# Revit family: Faucet-Kitchen_Sink-KOHLER-Artifacts-K-76519
name_source: partatom
category: Plumbing Fixtures
revit_build: Autodesk Revit 2015 (Build: 20140606_1530(x64)
units: mm (PartAtom-declared; Revit-internal decimal feet)

## types (8) — shared parameters
ADA Compliant = Yes
Assembly Code = D2020
CW Connection = Yes
Cold Water Inlet = Cold Water Inlet
Date Modified = 03/16/2018
Default Elevation = 36"
Faucet Hole Spacing = 8"
Flow Rate = 2 GPM
HW Connection = Yes
Height = 13 1/2"
Hot Water Inlet = Hot Water Inlet
Length = 8 1/2"
Manufacturer = KOHLER Co.
MasterFormat 1995 = 15410
MasterFormat 2004 = 22.41.39
Material = Premium Metal Construction
Pressure = 60.00 psi
Product Documentation Link = http://www.us.kohler.com
Product Name = Artifacts
Product Page URL = http://www.us.kohler.com
Spout Reach = 8 1/2"
URL = https://www.us.kohler.com
Vent Connection = No
Waste Connection = No
Waste Water Outlet = Waste Water Outlet

## per-type parameters (varying)
| type | Description | Finish | Lever Handle | Model | Prong Handle | Type |
| Prong Handles- CP- Polished Chrome | Deck-mount bridge kitchen sink faucet with prong handles and sidespray | Kohler-Metal-CP-Polished_Chrome | No | K-76519-3M-CP | Yes | 1 |
| Prong Handles- SN- Vibrant Polished Nickel | Deck-mount bridge kitchen sink faucet with prong handles and sidespray | Kohler-Metal-SN-Vibrant_Polished_Nickel | No | K-76519-3M-SN | Yes | 2 |
| Prong Handles- VS- Vibrant Stainless | Deck-mount bridge kitchen sink faucet with prong handles and sidespray | Kohler-Metal-VS-Vibrant_Stainless | No | K-76519-3M-VS | Yes | 3 |
| Prong Handles- 2BZ- Oil- Rubbed Bronze | Deck-mount bridge kitchen sink faucet with prong handles and sidespray | Kohler-Metal-2BZ-Oil_Rubbed_Bronze | No | K-76519-3M-2BZ | Yes | 4 |
| Lever Handles- CP- Polished Chrome | Deck-mount bridge kitchen sink faucet with lever handles and sidespray | Kohler-Metal-CP-Polished_Chrome | Yes | K-76519-4-CP | No | 5 |
| Lever Handles- SN- Vibrant Polished Nickel | Deck-mount bridge kitchen sink faucet with lever handles and sidespray | Kohler-Metal-SN-Vibrant_Polished_Nickel | Yes | K-76519-4-SN | No | 6 |
| Lever Handles- VS Vibrant Stainless | Deck-mount bridge kitchen sink faucet with lever handles and sidespray | Kohler-Metal-VS-Vibrant_Stainless | Yes | K-76519-4-VS | No | 7 |
| Lever Handles- 2BZ- Oil- Rubbed Bronze | Deck-mount bridge kitchen sink faucet with lever handles and sidespray | Kohler-Metal-2BZ-Oil_Rubbed_Bronze | Yes | K-76519-4-2BZ | No | 8 |

## geometry (parser evidence)
native form markers: Blend x2, Sweep x7
no freeform markers — native parametric forms only
